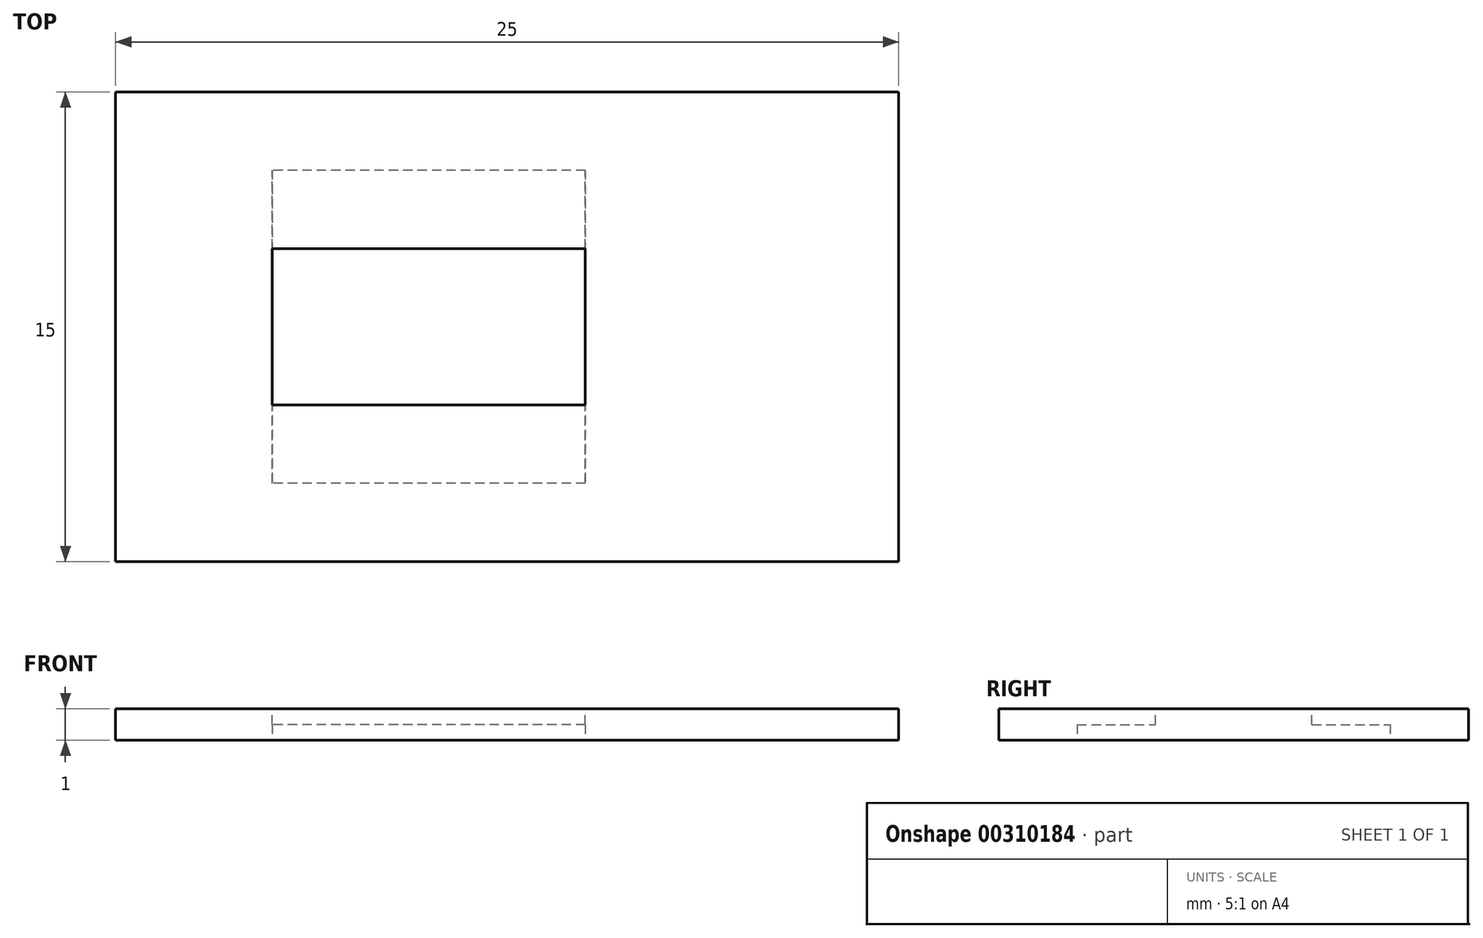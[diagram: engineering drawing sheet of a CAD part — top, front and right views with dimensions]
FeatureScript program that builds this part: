
annotation { "Feature Type Name" : "Feature", "Feature Type Description" : "" }
export const myFeature = defineFeature(function(context is Context, id is Id, definition is map)
    precondition{}
    {
        {
            var Q0;
            Q0=qCreatedBy(makeId("Top.planeOp"),FACE);
            var sketch = newSketch(context, id + "F0", { "sketchPlane" : qUnion([Q0])});
            skLineSegment(sketch, "E0.bottom", {"start": v(12.5, 7.5) * mm, "end": v(-12.5, 7.5) * mm});
            skLineSegment(sketch, "E0.top", {"start": v(12.5, -7.5) * mm, "end": v(-12.5, -7.5) * mm});
            skLineSegment(sketch, "E0.left", {"start": v(12.5, 7.5) * mm, "end": v(12.5, -7.5) * mm});
            skLineSegment(sketch, "E0.right", {"start": v(-12.5, 7.5) * mm, "end": v(-12.5, -7.5) * mm});
            skPoint(sketch, "E0.middle", {"position": v(0, 0) * mm});
            skSolve(sketch);
        }
        {
            var Q0;
            Q0=makeQuery(id+"F0.imprint","IMPRINT",FACE,{"disambiguationData":[TD([[makeQuery(id+"F0.imprint","IMPRINT",EDGE,{"derivedFrom":sQuery(id+"F0.wireOp",EDGE,"E0.bottom")}),1.0]])]});
            extrude(context, id + "F1", {"entities" : qUnion([Q0]), "oppositeDirection" : true, "depth" : 1 * mm});
        }
        {
            var Q0;
            Q0=makeQuery(id+"F1.opExtrude","CAP_FACE",FACE,{"disambiguationData":[OSD([sQuery(id+"F0.wireOp",EDGE,"E0.bottom"),sQuery(id+"F0.wireOp",EDGE,"E0.top"),sQuery(id+"F0.wireOp",EDGE,"E0.left"),sQuery(id+"F0.wireOp",EDGE,"E0.right")])],"isStart":true});
            var sketch = newSketch(context, id + "F2", { "sketchPlane" : qUnion([Q0])});
            skLineSegment(sketch, "E1.bottom", {"start": v(2.5, 2.5) * mm, "end": v(-7.5, 2.5) * mm});
            skLineSegment(sketch, "E1.top", {"start": v(2.5, -2.5) * mm, "end": v(-7.5, -2.5) * mm});
            skLineSegment(sketch, "E1.left", {"start": v(2.5, 2.5) * mm, "end": v(2.5, -2.5) * mm});
            skLineSegment(sketch, "E1.right", {"start": v(-7.5, 2.5) * mm, "end": v(-7.5, -2.5) * mm});
            skPoint(sketch, "E1.middle", {"position": v(0, 0) * mm});
            skSolve(sketch);
        }
        {
            var Q0;
            Q0=makeQuery(id+"F2.imprint","IMPRINT",FACE,{"disambiguationData":[TD([[makeQuery(id+"F2.imprint","IMPRINT",EDGE,{"derivedFrom":sQuery(id+"F2.wireOp",EDGE,"E1.bottom")}),1.0]])]});
            extrude(context, id + "F3", {"entities" : qUnion([Q0]), "operationType" : NewBodyOperationType.REMOVE, "oppositeDirection" : true, "depth" : 25.4 * mm});
        }
        {
            var Q0;
            Q0=makeQuery(id+"F1.opExtrude","CAP_FACE",FACE,{"disambiguationData":[OSD([sQuery(id+"F0.wireOp",EDGE,"E0.bottom"),sQuery(id+"F0.wireOp",EDGE,"E0.top"),sQuery(id+"F0.wireOp",EDGE,"E0.left"),sQuery(id+"F0.wireOp",EDGE,"E0.right")])],"isStart":false});
            var sketch = newSketch(context, id + "F4", { "sketchPlane" : qUnion([Q0])});
            skLineSegment(sketch, "E2.bottom", {"start": v(2.5, 5) * mm, "end": v(-7.5, 5) * mm});
            skLineSegment(sketch, "E2.top", {"start": v(2.5, -5) * mm, "end": v(-7.5, -5) * mm});
            skLineSegment(sketch, "E2.left", {"start": v(2.5, 5) * mm, "end": v(2.5, -5) * mm});
            skLineSegment(sketch, "E2.right", {"start": v(-7.5, 5) * mm, "end": v(-7.5, -5) * mm});
            skPoint(sketch, "E2.middle", {"position": v(-2.5, 0) * mm});
            skSolve(sketch);
        }
        {
            var Q0;
            {var subQ0=sQuery(id+"F4.wireOp",EDGE,"E2.bottom");Q0=makeQuery(id+"F4.imprint","IMPRINT",FACE,{"disambiguationData":[TD([[makeQuery(id+"F4.imprint","IMPRINT",EDGE,{"derivedFrom":subQ0}),1.0]])]});}
            var Q1;
            {var subQ0=sQuery(id+"F4.wireOp",EDGE,"E2.top");Q1=makeQuery(id+"F4.imprint","IMPRINT",FACE,{"disambiguationData":[TD([[makeQuery(id+"F4.imprint","IMPRINT",EDGE,{"derivedFrom":subQ0}),-1.0]])]});}
            extrude(context, id + "F5", {"entities" : qUnion([Q0, Q1]), "operationType" : NewBodyOperationType.REMOVE, "oppositeDirection" : true, "depth" : 0.5 * mm});
        }
    });
